# Revit family: Plumbing-Faucet-Sloan-Valve-EFX-280
name_source: partatom
category: Plumbing Fixtures
units: mm (PartAtom-declared; Revit-internal decimal feet)

## family parameters
Cut with Voids When Loaded = No
Host = Face
Maintain Annotation Orientation = No
OmniClass Number = 23.45.55.14
OmniClass Title = Single Faucets
Part Type = Normal
Room Calculation Point = No
Round Connector Dimension = Use Diameter
Shared = No

## types (8) — shared parameters
Assembly Code = D2010
CW Connection = Yes
CWFU = 1.5
Cold Water Connection Diameter = 0"
Depth = 6.47 "
Edition number = 1
HW Connection = Yes
HWFU = 1.5
Height = 6.47 "
Hot Water Connection Diameter = 0"
Hot Water Connector Description = Hot Water Connection
Keynote = 15410
Manufacturer = Sloan Valve
Product Material = Sloan Valve - Finish - Polished Chrome
Product data url = https://bimobject.com
URL = www.sloanvalve.com
Valve Pressure Drop = 0.00 psi
Vent Connection = No
Waste Connection = No
Width = 2 "
zero-valued in all types: Default Elevation, WFU

## per-type parameters (varying)
| type | Description | Part Number | Water Flow |
| EFX-280-TUR-ISM-CP-0.5GPM-MLM-IR-CO-FCT | Turbine Power Supply, Integrated Side Mixer, Polished Chrome Finish, 0.5 gpm, Multi-Laminar Spray, Infrared Sensor, BASYS® TurbinePowered Deck-Mounted Mid Body. | 3324369T | 1 GPM |
| EFX-280-TUR-ISM-CP-0.5GPM-MLM-IR-FCT | Turbine Power Supply, Integrated Side Mixer, Polished Chrome Finish, 0.5 gpm, Multi-Laminar Spray, Infrared Sensor, BASYS® TurbinePowered Deck-Mounted Mid Body. | 3324369 | 1 GPM |
| EFX-280-TUR-ISM-CP-1.5GPM-IR-FCT | Turbine Power Supply, Integrated Side Mixer, Polished Chrome Finish, 1.5 gpm, Aerated (installed) or Laminar (in box) Spray, Infrared Sensor, BASYS® Turbine-Powered Deck-Mounted Mid Body. | 3324368 | 2 GPM |
| EFX-280-TUR-TEE-CP-0.5GPM-MLM-IR-CO-FCT | Turbine Power Supply, Back-Check Tee, Polished Chrome Finish, 0.5 gpm, Multi-Laminar Spray, Infrared Sensor, BASYS® Turbine-Powered Deck-Mounted Mid Body. | 3324371T | 1 GPM |
| EFX-280-TUR-TEE-CP-0.5GPM-MLM-IR-FCT | Turbine Power Supply, Back-Check Tee, Polished Chrome Finish, 0.5 gpm, Multi-Laminar Spray, Infrared Sensor, BASYS® Turbine-Powered Deck-Mounted Mid Body. | 3324371 | 1 GPM |
| EFX-280-TUR-TEE-CP-1.5GPM-IR-FCT | Turbine Power Supply, Back-Check Tee, Polished Chrome Finish, 1.5 gpm, Aerated (installed) or Laminar (in box) Spray, Infrared Sensor, BASYS® Turbine-Powered Deck-Mounted Mid Body. | 3324370 | 2 GPM |
| EFX-280-TUR-ISM-CP-0.35GPM-MLM-IR-FCT | Turbine Power Supply, Integrated Side Mixer, Polished Chrome Finish, 0.35 gpm, Multi-Laminar Spray, Infrared Sensor, BASYS® TurbinePowered Deck-Mounted Mid Body. | 33243143 | 0 GPM |
| EFX-280-TUR-TEE-CP-0.35GPM-MLM-IR-FCT | Turbine Power Supply, Back-Check Tee, Polished Chrome Finish, 0.35 gpm, Multi-Laminar Spray, Infrared Sensor, BASYS® Turbine-Powered Deck-Mounted Mid Body. | 33243144 | 0 GPM |

note: column(s) folded — value = type name in every type: Model

## geometry (parser evidence)
native form markers: Sweep x8
no freeform markers — native parametric forms only
